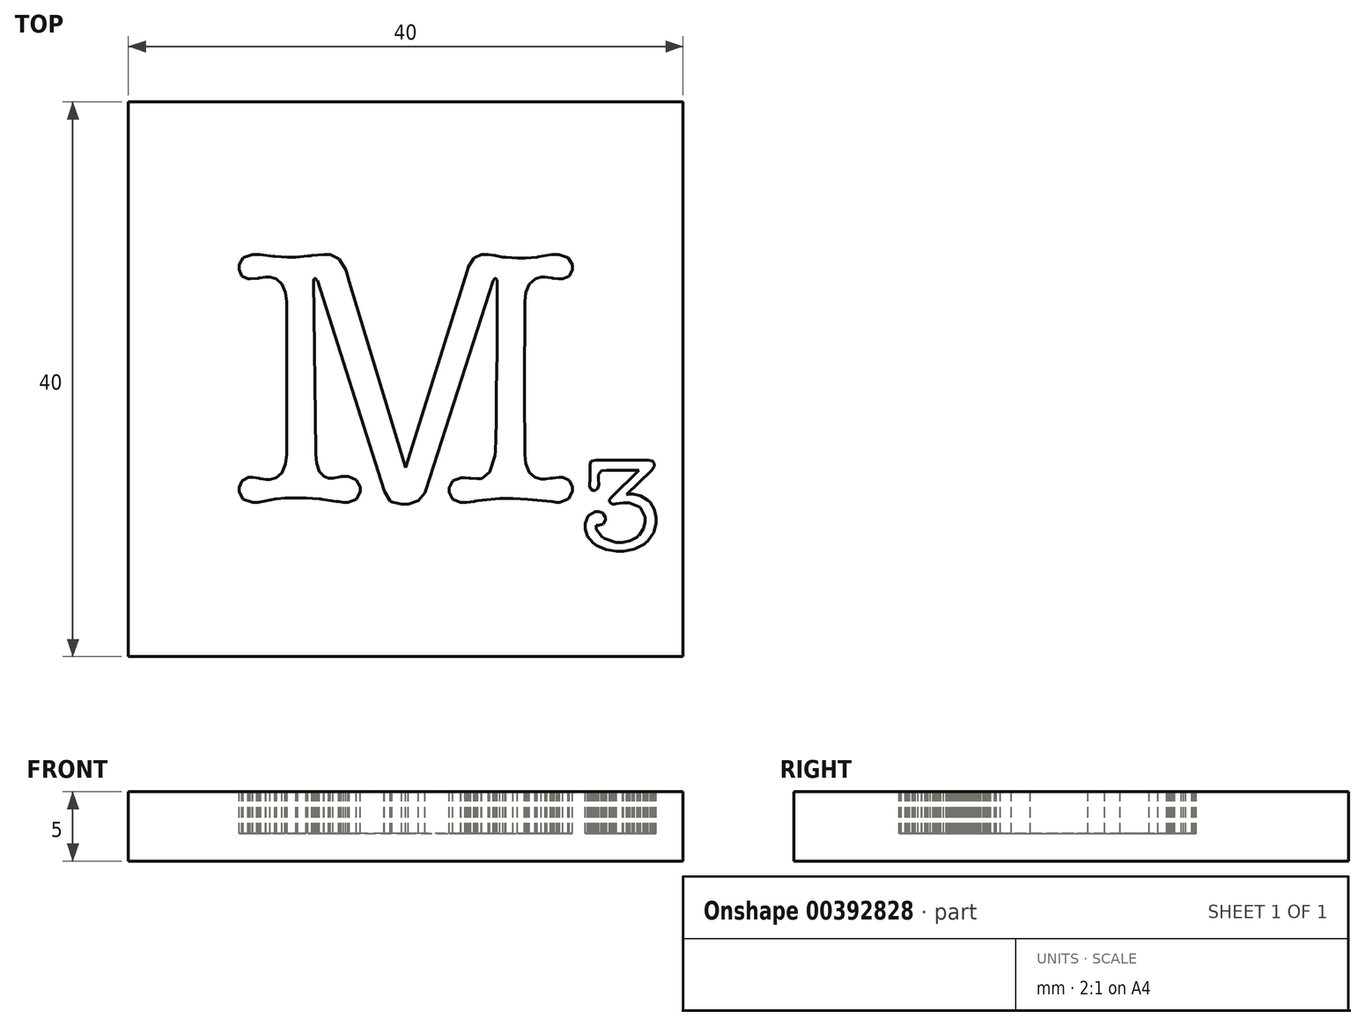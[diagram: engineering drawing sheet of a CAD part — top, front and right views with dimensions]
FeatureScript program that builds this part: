
annotation { "Feature Type Name" : "Feature", "Feature Type Description" : "" }
export const myFeature = defineFeature(function(context is Context, id is Id, definition is map)
    precondition{}
    {
        {
            var Q0;
            Q0=qCreatedBy(makeId("Top.planeOp"),FACE);
            var sketch = newSketch(context, id + "F0", { "sketchPlane" : qUnion([Q0])});
            skLineSegment(sketch, "E0.bottom", {"start": v(20, -20) * mm, "end": v(-20, -20) * mm});
            skLineSegment(sketch, "E0.top", {"start": v(20, 20) * mm, "end": v(-20, 20) * mm});
            skLineSegment(sketch, "E0.left", {"start": v(20, -20) * mm, "end": v(20, 20) * mm});
            skLineSegment(sketch, "E0.right", {"start": v(-20, -20) * mm, "end": v(-20, 20) * mm});
            skPoint(sketch, "E0.middle", {"position": v(0, 0) * mm});
            skSolve(sketch);
        }
        {
            var Q0;
            Q0=makeQuery(id+"F0.imprint","IMPRINT",FACE,{"disambiguationData":[TD([[makeQuery(id+"F0.imprint","IMPRINT",EDGE,{"derivedFrom":sQuery(id+"F0.wireOp",EDGE,"E0.bottom")}),-1.0]])]});
            extrude(context, id + "F1", {"entities" : qUnion([Q0]), "depth" : -5 * mm});
        }
        {
            var Q0;
            Q0=qCreatedBy(makeId("Top.planeOp"),FACE);
            var sketch = newSketch(context, id + "F2", { "sketchPlane" : qUnion([Q0])});
            skLineSegment(sketch, "E1", {"start": v(-4.09, 7.02) * mm, "end": v(-0.01, -6.36) * mm});
            skLineSegment(sketch, "E2", {"start": v(-0.01, -6.36) * mm, "end": v(4.46, 7.9) * mm});
            skLineSegment(sketch, "E3", {"start": v(4.46, 7.9) * mm, "end": v(4.51, 8.08) * mm});
            skLineSegment(sketch, "E4", {"start": v(4.51, 8.08) * mm, "end": v(4.93, 8.73) * mm});
            skLineSegment(sketch, "E5", {"start": v(4.93, 8.73) * mm, "end": v(5.47, 9) * mm});
            skLineSegment(sketch, "E6", {"start": v(5.47, 9) * mm, "end": v(5.65, 9) * mm});
            skLineSegment(sketch, "E7", {"start": v(5.65, 9) * mm, "end": v(5.78, 9) * mm});
            skLineSegment(sketch, "E8", {"start": v(5.78, 9) * mm, "end": v(5.95, 9) * mm});
            skLineSegment(sketch, "E9", {"start": v(5.95, 9) * mm, "end": v(6.4, 8.94) * mm});
            skLineSegment(sketch, "E10", {"start": v(6.4, 8.94) * mm, "end": v(6.47, 8.93) * mm});
            skLineSegment(sketch, "E11", {"start": v(6.47, 8.93) * mm, "end": v(6.56, 8.9) * mm});
            skLineSegment(sketch, "E12", {"start": v(6.56, 8.9) * mm, "end": v(7, 8.8) * mm});
            skLineSegment(sketch, "E13", {"start": v(7, 8.8) * mm, "end": v(7.16, 8.8) * mm});
            skLineSegment(sketch, "E14", {"start": v(7.16, 8.8) * mm, "end": v(7.23, 8.79) * mm});
            skLineSegment(sketch, "E15", {"start": v(7.23, 8.79) * mm, "end": v(8.05, 8.74) * mm});
            skLineSegment(sketch, "E16", {"start": v(8.05, 8.74) * mm, "end": v(8.32, 8.74) * mm});
            skLineSegment(sketch, "E17", {"start": v(8.32, 8.74) * mm, "end": v(8.63, 8.74) * mm});
            skLineSegment(sketch, "E18", {"start": v(8.63, 8.74) * mm, "end": v(9.49, 8.81) * mm});
            skLineSegment(sketch, "E19", {"start": v(9.49, 8.81) * mm, "end": v(9.56, 8.82) * mm});
            skLineSegment(sketch, "E20", {"start": v(9.56, 8.82) * mm, "end": v(10.5, 8.98) * mm});
            skLineSegment(sketch, "E21", {"start": v(10.5, 8.98) * mm, "end": v(10.5, 8.99) * mm});
            skLineSegment(sketch, "E22", {"start": v(10.5, 8.99) * mm, "end": v(10.73, 9) * mm});
            skLineSegment(sketch, "E23", {"start": v(10.73, 9) * mm, "end": v(10.8, 9) * mm});
            skLineSegment(sketch, "E24", {"start": v(10.8, 9) * mm, "end": v(11.03, 9) * mm});
            skLineSegment(sketch, "E25", {"start": v(11.03, 9) * mm, "end": v(11.72, 8.78) * mm});
            skLineSegment(sketch, "E26", {"start": v(11.72, 8.78) * mm, "end": v(12.03, 8.26) * mm});
            skLineSegment(sketch, "E27", {"start": v(12.03, 8.26) * mm, "end": v(12.03, 8.08) * mm});
            skLineSegment(sketch, "E28", {"start": v(12.03, 8.08) * mm, "end": v(12.03, 7.92) * mm});
            skLineSegment(sketch, "E29", {"start": v(12.03, 7.92) * mm, "end": v(11.81, 7.45) * mm});
            skLineSegment(sketch, "E30", {"start": v(11.81, 7.45) * mm, "end": v(11.34, 7.24) * mm});
            skLineSegment(sketch, "E31", {"start": v(11.34, 7.24) * mm, "end": v(11.18, 7.24) * mm});
            skLineSegment(sketch, "E32", {"start": v(11.18, 7.24) * mm, "end": v(11.02, 7.24) * mm});
            skLineSegment(sketch, "E33", {"start": v(11.02, 7.24) * mm, "end": v(10.62, 7.3) * mm});
            skLineSegment(sketch, "E34", {"start": v(10.62, 7.3) * mm, "end": v(10.56, 7.3) * mm});
            skLineSegment(sketch, "E35", {"start": v(10.56, 7.3) * mm, "end": v(10.49, 7.31) * mm});
            skLineSegment(sketch, "E36", {"start": v(10.49, 7.31) * mm, "end": v(10.07, 7.37) * mm});
            skLineSegment(sketch, "E37", {"start": v(10.07, 7.37) * mm, "end": v(9.93, 7.37) * mm});
            skLineSegment(sketch, "E38", {"start": v(9.93, 7.37) * mm, "end": v(9.79, 7.37) * mm});
            skLineSegment(sketch, "E39", {"start": v(9.79, 7.37) * mm, "end": v(9.34, 7.25) * mm});
            skLineSegment(sketch, "E40", {"start": v(9.34, 7.25) * mm, "end": v(8.92, 6.87) * mm});
            skLineSegment(sketch, "E41", {"start": v(8.92, 6.87) * mm, "end": v(8.67, 6.25) * mm});
            skLineSegment(sketch, "E42", {"start": v(8.67, 6.25) * mm, "end": v(8.59, 5.6) * mm});
            skLineSegment(sketch, "E43", {"start": v(8.59, 5.6) * mm, "end": v(8.59, 5.38) * mm});
            skLineSegment(sketch, "E44", {"start": v(8.59, 5.38) * mm, "end": v(8.59, 3.53) * mm});
            skLineSegment(sketch, "E45", {"start": v(8.59, 3.53) * mm, "end": v(8.56, 1.2) * mm});
            skLineSegment(sketch, "E46", {"start": v(8.56, 1.2) * mm, "end": v(8.56, -1.05) * mm});
            skLineSegment(sketch, "E47", {"start": v(8.56, -1.05) * mm, "end": v(8.59, -5.22) * mm});
            skLineSegment(sketch, "E48", {"start": v(8.59, -5.22) * mm, "end": v(8.59, -5.44) * mm});
            skLineSegment(sketch, "E49", {"start": v(8.59, -5.44) * mm, "end": v(8.67, -6.1) * mm});
            skLineSegment(sketch, "E50", {"start": v(8.67, -6.1) * mm, "end": v(8.92, -6.71) * mm});
            skLineSegment(sketch, "E51", {"start": v(8.92, -6.71) * mm, "end": v(9.33, -7.09) * mm});
            skLineSegment(sketch, "E52", {"start": v(9.33, -7.09) * mm, "end": v(9.76, -7.2) * mm});
            skLineSegment(sketch, "E53", {"start": v(9.76, -7.2) * mm, "end": v(9.9, -7.2) * mm});
            skLineSegment(sketch, "E54", {"start": v(9.9, -7.2) * mm, "end": v(10.05, -7.2) * mm});
            skLineSegment(sketch, "E55", {"start": v(10.05, -7.2) * mm, "end": v(10.44, -7.14) * mm});
            skLineSegment(sketch, "E56", {"start": v(10.44, -7.14) * mm, "end": v(10.5, -7.13) * mm});
            skLineSegment(sketch, "E57", {"start": v(10.5, -7.13) * mm, "end": v(10.59, -7.12) * mm});
            skLineSegment(sketch, "E58", {"start": v(10.59, -7.12) * mm, "end": v(11.03, -7.08) * mm});
            skLineSegment(sketch, "E59", {"start": v(11.03, -7.08) * mm, "end": v(11.18, -7.08) * mm});
            skLineSegment(sketch, "E60", {"start": v(11.18, -7.08) * mm, "end": v(11.34, -7.08) * mm});
            skLineSegment(sketch, "E61", {"start": v(11.34, -7.08) * mm, "end": v(11.81, -7.29) * mm});
            skLineSegment(sketch, "E62", {"start": v(11.81, -7.29) * mm, "end": v(12.03, -7.76) * mm});
            skLineSegment(sketch, "E63", {"start": v(12.03, -7.76) * mm, "end": v(12.03, -7.92) * mm});
            skLineSegment(sketch, "E64", {"start": v(12.03, -7.92) * mm, "end": v(12.03, -8.1) * mm});
            skLineSegment(sketch, "E65", {"start": v(12.03, -8.1) * mm, "end": v(11.74, -8.64) * mm});
            skLineSegment(sketch, "E66", {"start": v(11.74, -8.64) * mm, "end": v(11.1, -8.88) * mm});
            skLineSegment(sketch, "E67", {"start": v(11.1, -8.88) * mm, "end": v(10.89, -8.88) * mm});
            skLineSegment(sketch, "E68", {"start": v(10.89, -8.88) * mm, "end": v(10.56, -8.83) * mm});
            skLineSegment(sketch, "E69", {"start": v(10.56, -8.83) * mm, "end": v(10.5, -8.82) * mm});
            skLineSegment(sketch, "E70", {"start": v(10.5, -8.82) * mm, "end": v(10.19, -8.79) * mm});
            skLineSegment(sketch, "E71", {"start": v(10.19, -8.79) * mm, "end": v(8.8, -8.66) * mm});
            skLineSegment(sketch, "E72", {"start": v(8.8, -8.66) * mm, "end": v(7.75, -8.61) * mm});
            skLineSegment(sketch, "E73", {"start": v(7.75, -8.61) * mm, "end": v(7.4, -8.61) * mm});
            skLineSegment(sketch, "E74", {"start": v(7.4, -8.61) * mm, "end": v(6.8, -8.61) * mm});
            skLineSegment(sketch, "E75", {"start": v(6.8, -8.61) * mm, "end": v(5.2, -8.77) * mm});
            skLineSegment(sketch, "E76", {"start": v(5.2, -8.77) * mm, "end": v(5.01, -8.8) * mm});
            skLineSegment(sketch, "E77", {"start": v(5.01, -8.8) * mm, "end": v(4.93, -8.8) * mm});
            skLineSegment(sketch, "E78", {"start": v(4.93, -8.8) * mm, "end": v(4.36, -8.88) * mm});
            skLineSegment(sketch, "E79", {"start": v(4.36, -8.88) * mm, "end": v(4.17, -8.88) * mm});
            skLineSegment(sketch, "E80", {"start": v(4.17, -8.88) * mm, "end": v(3.97, -8.88) * mm});
            skLineSegment(sketch, "E81", {"start": v(3.97, -8.88) * mm, "end": v(3.4, -8.66) * mm});
            skLineSegment(sketch, "E82", {"start": v(3.4, -8.66) * mm, "end": v(3.13, -8.17) * mm});
            skLineSegment(sketch, "E83", {"start": v(3.13, -8.17) * mm, "end": v(3.13, -8) * mm});
            skLineSegment(sketch, "E84", {"start": v(3.13, -8) * mm, "end": v(3.13, -7.83) * mm});
            skLineSegment(sketch, "E85", {"start": v(3.13, -7.83) * mm, "end": v(3.4, -7.33) * mm});
            skLineSegment(sketch, "E86", {"start": v(3.4, -7.33) * mm, "end": v(4, -7.1) * mm});
            skLineSegment(sketch, "E87", {"start": v(4, -7.1) * mm, "end": v(4.2, -7.1) * mm});
            skLineSegment(sketch, "E88", {"start": v(4.2, -7.1) * mm, "end": v(4.3, -7.1) * mm});
            skLineSegment(sketch, "E89", {"start": v(4.3, -7.1) * mm, "end": v(4.57, -7.13) * mm});
            skLineSegment(sketch, "E90", {"start": v(4.57, -7.13) * mm, "end": v(4.59, -7.13) * mm});
            skLineSegment(sketch, "E91", {"start": v(4.59, -7.13) * mm, "end": v(4.69, -7.14) * mm});
            skLineSegment(sketch, "E92", {"start": v(4.69, -7.14) * mm, "end": v(5.13, -7.18) * mm});
            skLineSegment(sketch, "E93", {"start": v(5.13, -7.18) * mm, "end": v(5.28, -7.18) * mm});
            skLineSegment(sketch, "E94", {"start": v(5.28, -7.18) * mm, "end": v(5.47, -7.18) * mm});
            skLineSegment(sketch, "E95", {"start": v(5.47, -7.18) * mm, "end": v(6.05, -6.69) * mm});
            skLineSegment(sketch, "E96", {"start": v(6.05, -6.69) * mm, "end": v(6.43, -5.53) * mm});
            skLineSegment(sketch, "E97", {"start": v(6.43, -5.53) * mm, "end": v(6.47, -5.2) * mm});
            skLineSegment(sketch, "E98", {"start": v(6.47, -5.2) * mm, "end": v(6.48, -5.13) * mm});
            skLineSegment(sketch, "E99", {"start": v(6.48, -5.13) * mm, "end": v(6.5, -4.31) * mm});
            skLineSegment(sketch, "E100", {"start": v(6.5, -4.31) * mm, "end": v(6.52, -2.95) * mm});
            skLineSegment(sketch, "E101", {"start": v(6.52, -2.95) * mm, "end": v(6.52, -2.5) * mm});
            skLineSegment(sketch, "E102", {"start": v(6.52, -2.5) * mm, "end": v(6.52, -2.23) * mm});
            skLineSegment(sketch, "E103", {"start": v(6.52, -2.23) * mm, "end": v(6.53, -1.43) * mm});
            skLineSegment(sketch, "E104", {"start": v(6.53, -1.43) * mm, "end": v(6.54, -0.24) * mm});
            skLineSegment(sketch, "E105", {"start": v(6.54, -0.24) * mm, "end": v(6.55, 0.04) * mm});
            skLineSegment(sketch, "E106", {"start": v(6.55, 0.04) * mm, "end": v(6.6, 2.42) * mm});
            skLineSegment(sketch, "E107", {"start": v(6.6, 2.42) * mm, "end": v(6.6, 7.1) * mm});
            skLineSegment(sketch, "E108", {"start": v(6.6, 7.1) * mm, "end": v(6.6, 7.14) * mm});
            skLineSegment(sketch, "E109", {"start": v(6.6, 7.14) * mm, "end": v(6.5, 7.26) * mm});
            skLineSegment(sketch, "E110", {"start": v(6.5, 7.26) * mm, "end": v(6.47, 7.26) * mm});
            skLineSegment(sketch, "E111", {"start": v(6.47, 7.26) * mm, "end": v(6.43, 7.26) * mm});
            skLineSegment(sketch, "E112", {"start": v(6.43, 7.26) * mm, "end": v(6.32, 7.13) * mm});
            skLineSegment(sketch, "E113", {"start": v(6.32, 7.13) * mm, "end": v(6.3, 7.1) * mm});
            skLineSegment(sketch, "E114", {"start": v(6.3, 7.1) * mm, "end": v(1.44, -8) * mm});
            skLineSegment(sketch, "E115", {"start": v(1.44, -8) * mm, "end": v(1.39, -8.17) * mm});
            skLineSegment(sketch, "E116", {"start": v(1.39, -8.17) * mm, "end": v(0.91, -8.76) * mm});
            skLineSegment(sketch, "E117", {"start": v(0.91, -8.76) * mm, "end": v(0.2, -9) * mm});
            skLineSegment(sketch, "E118", {"start": v(0.2, -9) * mm, "end": v(-0.04, -9) * mm});
            skLineSegment(sketch, "E119", {"start": v(-0.04, -9) * mm, "end": v(-0.3, -9) * mm});
            skLineSegment(sketch, "E120", {"start": v(-0.3, -9) * mm, "end": v(-1, -8.84) * mm});
            skLineSegment(sketch, "E121", {"start": v(-1, -8.84) * mm, "end": v(-1.06, -8.81) * mm});
            skLineSegment(sketch, "E122", {"start": v(-1.06, -8.81) * mm, "end": v(-1.11, -8.78) * mm});
            skLineSegment(sketch, "E123", {"start": v(-1.11, -8.78) * mm, "end": v(-1.54, -8.1) * mm});
            skLineSegment(sketch, "E124", {"start": v(-1.54, -8.1) * mm, "end": v(-1.57, -8) * mm});
            skLineSegment(sketch, "E125", {"start": v(-1.57, -8) * mm, "end": v(-6.36, 7.1) * mm});
            skLineSegment(sketch, "E126", {"start": v(-6.36, 7.1) * mm, "end": v(-6.38, 7.13) * mm});
            skLineSegment(sketch, "E127", {"start": v(-6.38, 7.13) * mm, "end": v(-6.5, 7.26) * mm});
            skLineSegment(sketch, "E128", {"start": v(-6.5, 7.26) * mm, "end": v(-6.55, 7.26) * mm});
            skLineSegment(sketch, "E129", {"start": v(-6.55, 7.26) * mm, "end": v(-6.58, 7.26) * mm});
            skLineSegment(sketch, "E130", {"start": v(-6.58, 7.26) * mm, "end": v(-6.66, 7.14) * mm});
            skLineSegment(sketch, "E131", {"start": v(-6.66, 7.14) * mm, "end": v(-6.66, 7.1) * mm});
            skLineSegment(sketch, "E132", {"start": v(-6.66, 7.1) * mm, "end": v(-6.5, -5.2) * mm});
            skLineSegment(sketch, "E133", {"start": v(-6.5, -5.2) * mm, "end": v(-6.5, -5.4) * mm});
            skLineSegment(sketch, "E134", {"start": v(-6.5, -5.4) * mm, "end": v(-6.42, -6.04) * mm});
            skLineSegment(sketch, "E135", {"start": v(-6.42, -6.04) * mm, "end": v(-6.22, -6.65) * mm});
            skLineSegment(sketch, "E136", {"start": v(-6.22, -6.65) * mm, "end": v(-5.9, -7) * mm});
            skLineSegment(sketch, "E137", {"start": v(-5.9, -7) * mm, "end": v(-5.55, -7.13) * mm});
            skLineSegment(sketch, "E138", {"start": v(-5.55, -7.13) * mm, "end": v(-5.44, -7.13) * mm});
            skLineSegment(sketch, "E139", {"start": v(-5.44, -7.13) * mm, "end": v(-5.24, -7.13) * mm});
            skLineSegment(sketch, "E140", {"start": v(-5.24, -7.13) * mm, "end": v(-4.73, -7.04) * mm});
            skLineSegment(sketch, "E141", {"start": v(-4.73, -7.04) * mm, "end": v(-4.64, -7.02) * mm});
            skLineSegment(sketch, "E142", {"start": v(-4.64, -7.02) * mm, "end": v(-4.33, -7.02) * mm});
            skLineSegment(sketch, "E143", {"start": v(-4.33, -7.02) * mm, "end": v(-4.13, -7.02) * mm});
            skLineSegment(sketch, "E144", {"start": v(-4.13, -7.02) * mm, "end": v(-3.55, -7.26) * mm});
            skLineSegment(sketch, "E145", {"start": v(-3.55, -7.26) * mm, "end": v(-3.3, -7.78) * mm});
            skLineSegment(sketch, "E146", {"start": v(-3.3, -7.78) * mm, "end": v(-3.3, -7.95) * mm});
            skLineSegment(sketch, "E147", {"start": v(-3.3, -7.95) * mm, "end": v(-3.3, -8.12) * mm});
            skLineSegment(sketch, "E148", {"start": v(-3.3, -8.12) * mm, "end": v(-3.56, -8.65) * mm});
            skLineSegment(sketch, "E149", {"start": v(-3.56, -8.65) * mm, "end": v(-4.15, -8.88) * mm});
            skLineSegment(sketch, "E150", {"start": v(-4.15, -8.88) * mm, "end": v(-4.35, -8.88) * mm});
            skLineSegment(sketch, "E151", {"start": v(-4.35, -8.88) * mm, "end": v(-4.5, -8.88) * mm});
            skLineSegment(sketch, "E152", {"start": v(-4.5, -8.88) * mm, "end": v(-4.85, -8.83) * mm});
            skLineSegment(sketch, "E153", {"start": v(-4.85, -8.83) * mm, "end": v(-4.9, -8.82) * mm});
            skLineSegment(sketch, "E154", {"start": v(-4.9, -8.82) * mm, "end": v(-5, -8.81) * mm});
            skLineSegment(sketch, "E155", {"start": v(-5, -8.81) * mm, "end": v(-6.04, -8.65) * mm});
            skLineSegment(sketch, "E156", {"start": v(-6.04, -8.65) * mm, "end": v(-6.15, -8.64) * mm});
            skLineSegment(sketch, "E157", {"start": v(-6.15, -8.64) * mm, "end": v(-6.24, -8.62) * mm});
            skLineSegment(sketch, "E158", {"start": v(-6.24, -8.62) * mm, "end": v(-7.19, -8.56) * mm});
            skLineSegment(sketch, "E159", {"start": v(-7.19, -8.56) * mm, "end": v(-7.5, -8.56) * mm});
            skLineSegment(sketch, "E160", {"start": v(-7.5, -8.56) * mm, "end": v(-7.8, -8.56) * mm});
            skLineSegment(sketch, "E161", {"start": v(-7.8, -8.56) * mm, "end": v(-8.7, -8.58) * mm});
            skLineSegment(sketch, "E162", {"start": v(-8.7, -8.58) * mm, "end": v(-9.3, -8.62) * mm});
            skLineSegment(sketch, "E163", {"start": v(-9.3, -8.62) * mm, "end": v(-9.38, -8.64) * mm});
            skLineSegment(sketch, "E164", {"start": v(-9.38, -8.64) * mm, "end": v(-10.5, -8.85) * mm});
            skLineSegment(sketch, "E165", {"start": v(-10.5, -8.85) * mm, "end": v(-10.53, -8.85) * mm});
            skLineSegment(sketch, "E166", {"start": v(-10.53, -8.85) * mm, "end": v(-10.63, -8.87) * mm});
            skLineSegment(sketch, "E167", {"start": v(-10.63, -8.87) * mm, "end": v(-10.65, -8.88) * mm});
            skLineSegment(sketch, "E168", {"start": v(-10.65, -8.88) * mm, "end": v(-10.8, -8.88) * mm});
            skLineSegment(sketch, "E169", {"start": v(-10.8, -8.88) * mm, "end": v(-11.04, -8.88) * mm});
            skLineSegment(sketch, "E170", {"start": v(-11.04, -8.88) * mm, "end": v(-11.72, -8.65) * mm});
            skLineSegment(sketch, "E171", {"start": v(-11.72, -8.65) * mm, "end": v(-12.03, -8.12) * mm});
            skLineSegment(sketch, "E172", {"start": v(-12.03, -8.12) * mm, "end": v(-12.03, -7.95) * mm});
            skLineSegment(sketch, "E173", {"start": v(-12.03, -7.95) * mm, "end": v(-12.03, -7.8) * mm});
            skLineSegment(sketch, "E174", {"start": v(-12.03, -7.8) * mm, "end": v(-11.83, -7.37) * mm});
            skLineSegment(sketch, "E175", {"start": v(-11.83, -7.37) * mm, "end": v(-11.79, -7.33) * mm});
            skLineSegment(sketch, "E176", {"start": v(-11.79, -7.33) * mm, "end": v(-11.75, -7.29) * mm});
            skLineSegment(sketch, "E177", {"start": v(-11.75, -7.29) * mm, "end": v(-11.34, -7.08) * mm});
            skLineSegment(sketch, "E178", {"start": v(-11.34, -7.08) * mm, "end": v(-11.2, -7.08) * mm});
            skLineSegment(sketch, "E179", {"start": v(-11.2, -7.08) * mm, "end": v(-11.03, -7.08) * mm});
            skLineSegment(sketch, "E180", {"start": v(-11.03, -7.08) * mm, "end": v(-10.58, -7.14) * mm});
            skLineSegment(sketch, "E181", {"start": v(-10.58, -7.14) * mm, "end": v(-10.52, -7.16) * mm});
            skLineSegment(sketch, "E182", {"start": v(-10.52, -7.16) * mm, "end": v(-10.45, -7.17) * mm});
            skLineSegment(sketch, "E183", {"start": v(-10.45, -7.17) * mm, "end": v(-10.06, -7.24) * mm});
            skLineSegment(sketch, "E184", {"start": v(-10.06, -7.24) * mm, "end": v(-9.93, -7.24) * mm});
            skLineSegment(sketch, "E185", {"start": v(-9.93, -7.24) * mm, "end": v(-9.79, -7.24) * mm});
            skLineSegment(sketch, "E186", {"start": v(-9.79, -7.24) * mm, "end": v(-9.35, -7.11) * mm});
            skLineSegment(sketch, "E187", {"start": v(-9.35, -7.11) * mm, "end": v(-8.92, -6.74) * mm});
            skLineSegment(sketch, "E188", {"start": v(-8.92, -6.74) * mm, "end": v(-8.67, -6.12) * mm});
            skLineSegment(sketch, "E189", {"start": v(-8.67, -6.12) * mm, "end": v(-8.59, -5.47) * mm});
            skLineSegment(sketch, "E190", {"start": v(-8.59, -5.47) * mm, "end": v(-8.59, -5.25) * mm});
            skLineSegment(sketch, "E191", {"start": v(-8.59, -5.25) * mm, "end": v(-8.59, 5.38) * mm});
            skLineSegment(sketch, "E192", {"start": v(-8.59, 5.38) * mm, "end": v(-8.59, 5.6) * mm});
            skLineSegment(sketch, "E193", {"start": v(-8.59, 5.6) * mm, "end": v(-8.67, 6.25) * mm});
            skLineSegment(sketch, "E194", {"start": v(-8.67, 6.25) * mm, "end": v(-8.92, 6.87) * mm});
            skLineSegment(sketch, "E195", {"start": v(-8.92, 6.87) * mm, "end": v(-9.35, 7.25) * mm});
            skLineSegment(sketch, "E196", {"start": v(-9.35, 7.25) * mm, "end": v(-9.79, 7.37) * mm});
            skLineSegment(sketch, "E197", {"start": v(-9.79, 7.37) * mm, "end": v(-9.93, 7.37) * mm});
            skLineSegment(sketch, "E198", {"start": v(-9.93, 7.37) * mm, "end": v(-10.1, 7.37) * mm});
            skLineSegment(sketch, "E199", {"start": v(-10.1, 7.37) * mm, "end": v(-10.5, 7.31) * mm});
            skLineSegment(sketch, "E200", {"start": v(-10.5, 7.31) * mm, "end": v(-10.57, 7.3) * mm});
            skLineSegment(sketch, "E201", {"start": v(-10.57, 7.3) * mm, "end": v(-10.64, 7.3) * mm});
            skLineSegment(sketch, "E202", {"start": v(-10.64, 7.3) * mm, "end": v(-11.2, 7.24) * mm});
            skLineSegment(sketch, "E203", {"start": v(-11.2, 7.24) * mm, "end": v(-11.36, 7.24) * mm});
            skLineSegment(sketch, "E204", {"start": v(-11.36, 7.24) * mm, "end": v(-11.82, 7.45) * mm});
            skLineSegment(sketch, "E205", {"start": v(-11.82, 7.45) * mm, "end": v(-12.03, 7.92) * mm});
            skLineSegment(sketch, "E206", {"start": v(-12.03, 7.92) * mm, "end": v(-12.03, 8.08) * mm});
            skLineSegment(sketch, "E207", {"start": v(-12.03, 8.08) * mm, "end": v(-12.03, 8.26) * mm});
            skLineSegment(sketch, "E208", {"start": v(-12.03, 8.26) * mm, "end": v(-11.73, 8.78) * mm});
            skLineSegment(sketch, "E209", {"start": v(-11.73, 8.78) * mm, "end": v(-11.06, 9) * mm});
            skLineSegment(sketch, "E210", {"start": v(-11.06, 9) * mm, "end": v(-10.83, 9) * mm});
            skLineSegment(sketch, "E211", {"start": v(-10.83, 9) * mm, "end": v(-10.75, 9) * mm});
            skLineSegment(sketch, "E212", {"start": v(-10.75, 9) * mm, "end": v(-10.53, 8.99) * mm});
            skLineSegment(sketch, "E213", {"start": v(-10.53, 8.99) * mm, "end": v(-10.5, 8.98) * mm});
            skLineSegment(sketch, "E214", {"start": v(-10.5, 8.98) * mm, "end": v(-9.57, 8.88) * mm});
            skLineSegment(sketch, "E215", {"start": v(-9.57, 8.88) * mm, "end": v(-9.45, 8.86) * mm});
            skLineSegment(sketch, "E216", {"start": v(-9.45, 8.86) * mm, "end": v(-8.57, 8.8) * mm});
            skLineSegment(sketch, "E217", {"start": v(-8.57, 8.8) * mm, "end": v(-8.27, 8.8) * mm});
            skLineSegment(sketch, "E218", {"start": v(-8.27, 8.8) * mm, "end": v(-7.93, 8.8) * mm});
            skLineSegment(sketch, "E219", {"start": v(-7.93, 8.8) * mm, "end": v(-7.05, 8.89) * mm});
            skLineSegment(sketch, "E220", {"start": v(-7.05, 8.89) * mm, "end": v(-6.9, 8.9) * mm});
            skLineSegment(sketch, "E221", {"start": v(-6.9, 8.9) * mm, "end": v(-6.76, 8.92) * mm});
            skLineSegment(sketch, "E222", {"start": v(-6.76, 8.92) * mm, "end": v(-5.93, 9) * mm});
            skLineSegment(sketch, "E223", {"start": v(-5.93, 9) * mm, "end": v(-5.65, 9) * mm});
            skLineSegment(sketch, "E224", {"start": v(-5.65, 9) * mm, "end": v(-5.44, 9) * mm});
            skLineSegment(sketch, "E225", {"start": v(-5.44, 9) * mm, "end": v(-4.8, 8.69) * mm});
            skLineSegment(sketch, "E226", {"start": v(-4.8, 8.69) * mm, "end": v(-4.33, 7.93) * mm});
            skLineSegment(sketch, "E227", {"start": v(-4.33, 7.93) * mm, "end": v(-4.27, 7.71) * mm});
            skLineSegment(sketch, "E228", {"start": v(-4.27, 7.71) * mm, "end": v(-4.09, 7.02) * mm});
            skSolve(sketch);
        }
        {
            var Q0;
            Q0=qCreatedBy(makeId("Top.planeOp"),FACE);
            var sketch = newSketch(context, id + "F3", { "sketchPlane" : qUnion([Q0])});
            skLineSegment(sketch, "E229", {"start": v(14.85, -8.5) * mm, "end": v(16.83, -6.56) * mm});
            skLineSegment(sketch, "E230", {"start": v(16.83, -6.56) * mm, "end": v(14.62, -6.56) * mm});
            skLineSegment(sketch, "E231", {"start": v(14.62, -6.56) * mm, "end": v(14.5, -6.56) * mm});
            skLineSegment(sketch, "E232", {"start": v(14.5, -6.56) * mm, "end": v(14.15, -6.6) * mm});
            skLineSegment(sketch, "E233", {"start": v(14.15, -6.6) * mm, "end": v(14.13, -6.6) * mm});
            skLineSegment(sketch, "E234", {"start": v(14.13, -6.6) * mm, "end": v(14.09, -6.62) * mm});
            skLineSegment(sketch, "E235", {"start": v(14.09, -6.62) * mm, "end": v(13.89, -6.9) * mm});
            skLineSegment(sketch, "E236", {"start": v(13.89, -6.9) * mm, "end": v(13.89, -6.98) * mm});
            skLineSegment(sketch, "E237", {"start": v(13.89, -6.98) * mm, "end": v(13.89, -7.05) * mm});
            skLineSegment(sketch, "E238", {"start": v(13.89, -7.05) * mm, "end": v(13.9, -7.23) * mm});
            skLineSegment(sketch, "E239", {"start": v(13.9, -7.23) * mm, "end": v(13.9, -7.26) * mm});
            skLineSegment(sketch, "E240", {"start": v(13.9, -7.26) * mm, "end": v(13.9, -7.29) * mm});
            skLineSegment(sketch, "E241", {"start": v(13.9, -7.29) * mm, "end": v(13.93, -7.47) * mm});
            skLineSegment(sketch, "E242", {"start": v(13.93, -7.47) * mm, "end": v(13.93, -7.53) * mm});
            skLineSegment(sketch, "E243", {"start": v(13.93, -7.53) * mm, "end": v(13.93, -7.63) * mm});
            skLineSegment(sketch, "E244", {"start": v(13.93, -7.63) * mm, "end": v(13.84, -7.9) * mm});
            skLineSegment(sketch, "E245", {"start": v(13.84, -7.9) * mm, "end": v(13.65, -8.03) * mm});
            skLineSegment(sketch, "E246", {"start": v(13.65, -8.03) * mm, "end": v(13.6, -8.03) * mm});
            skLineSegment(sketch, "E247", {"start": v(13.6, -8.03) * mm, "end": v(13.53, -8.03) * mm});
            skLineSegment(sketch, "E248", {"start": v(13.53, -8.03) * mm, "end": v(13.35, -7.93) * mm});
            skLineSegment(sketch, "E249", {"start": v(13.35, -7.93) * mm, "end": v(13.27, -7.7) * mm});
            skLineSegment(sketch, "E250", {"start": v(13.27, -7.7) * mm, "end": v(13.27, -7.62) * mm});
            skLineSegment(sketch, "E251", {"start": v(13.27, -7.62) * mm, "end": v(13.27, -7.53) * mm});
            skLineSegment(sketch, "E252", {"start": v(13.27, -7.53) * mm, "end": v(13.28, -7.3) * mm});
            skLineSegment(sketch, "E253", {"start": v(13.28, -7.3) * mm, "end": v(13.28, -7.27) * mm});
            skLineSegment(sketch, "E254", {"start": v(13.28, -7.27) * mm, "end": v(13.28, -7.23) * mm});
            skLineSegment(sketch, "E255", {"start": v(13.28, -7.23) * mm, "end": v(13.3, -6.92) * mm});
            skLineSegment(sketch, "E256", {"start": v(13.3, -6.92) * mm, "end": v(13.3, -6.82) * mm});
            skLineSegment(sketch, "E257", {"start": v(13.3, -6.82) * mm, "end": v(13.29, -6.55) * mm});
            skLineSegment(sketch, "E258", {"start": v(13.29, -6.55) * mm, "end": v(13.29, -6.52) * mm});
            skLineSegment(sketch, "E259", {"start": v(13.29, -6.52) * mm, "end": v(13.29, -6.5) * mm});
            skLineSegment(sketch, "E260", {"start": v(13.29, -6.5) * mm, "end": v(13.28, -6.3) * mm});
            skLineSegment(sketch, "E261", {"start": v(13.28, -6.3) * mm, "end": v(13.28, -6.23) * mm});
            skLineSegment(sketch, "E262", {"start": v(13.28, -6.23) * mm, "end": v(13.28, -6.15) * mm});
            skLineSegment(sketch, "E263", {"start": v(13.28, -6.15) * mm, "end": v(13.36, -5.92) * mm});
            skLineSegment(sketch, "E264", {"start": v(13.36, -5.92) * mm, "end": v(13.37, -5.9) * mm});
            skLineSegment(sketch, "E265", {"start": v(13.37, -5.9) * mm, "end": v(13.39, -5.9) * mm});
            skLineSegment(sketch, "E266", {"start": v(13.39, -5.9) * mm, "end": v(13.73, -5.85) * mm});
            skLineSegment(sketch, "E267", {"start": v(13.73, -5.85) * mm, "end": v(13.85, -5.85) * mm});
            skLineSegment(sketch, "E268", {"start": v(13.85, -5.85) * mm, "end": v(16.2, -5.85) * mm});
            skLineSegment(sketch, "E269", {"start": v(16.2, -5.85) * mm, "end": v(16.35, -5.85) * mm});
            skLineSegment(sketch, "E270", {"start": v(16.35, -5.85) * mm, "end": v(16.76, -5.83) * mm});
            skLineSegment(sketch, "E271", {"start": v(16.76, -5.83) * mm, "end": v(16.84, -5.83) * mm});
            skLineSegment(sketch, "E272", {"start": v(16.84, -5.83) * mm, "end": v(16.88, -5.83) * mm});
            skLineSegment(sketch, "E273", {"start": v(16.88, -5.83) * mm, "end": v(17.25, -5.82) * mm});
            skLineSegment(sketch, "E274", {"start": v(17.25, -5.82) * mm, "end": v(17.37, -5.82) * mm});
            skLineSegment(sketch, "E275", {"start": v(17.37, -5.82) * mm, "end": v(17.48, -5.82) * mm});
            skLineSegment(sketch, "E276", {"start": v(17.48, -5.82) * mm, "end": v(17.8, -5.9) * mm});
            skLineSegment(sketch, "E277", {"start": v(17.8, -5.9) * mm, "end": v(17.94, -6.1) * mm});
            skLineSegment(sketch, "E278", {"start": v(17.94, -6.1) * mm, "end": v(17.94, -6.16) * mm});
            skLineSegment(sketch, "E279", {"start": v(17.94, -6.16) * mm, "end": v(17.94, -6.27) * mm});
            skLineSegment(sketch, "E280", {"start": v(17.94, -6.27) * mm, "end": v(17.74, -6.57) * mm});
            skLineSegment(sketch, "E281", {"start": v(17.74, -6.57) * mm, "end": v(17.7, -6.6) * mm});
            skLineSegment(sketch, "E282", {"start": v(17.7, -6.6) * mm, "end": v(15.95, -8.3) * mm});
            skLineSegment(sketch, "E283", {"start": v(15.95, -8.3) * mm, "end": v(15.98, -8.3) * mm});
            skLineSegment(sketch, "E284", {"start": v(15.98, -8.3) * mm, "end": v(16.08, -8.29) * mm});
            skLineSegment(sketch, "E285", {"start": v(16.08, -8.29) * mm, "end": v(16.1, -8.29) * mm});
            skLineSegment(sketch, "E286", {"start": v(16.1, -8.29) * mm, "end": v(16.22, -8.29) * mm});
            skLineSegment(sketch, "E287", {"start": v(16.22, -8.29) * mm, "end": v(16.4, -8.29) * mm});
            skLineSegment(sketch, "E288", {"start": v(16.4, -8.29) * mm, "end": v(16.96, -8.41) * mm});
            skLineSegment(sketch, "E289", {"start": v(16.96, -8.41) * mm, "end": v(17.46, -8.72) * mm});
            skLineSegment(sketch, "E290", {"start": v(17.46, -8.72) * mm, "end": v(17.55, -8.8) * mm});
            skLineSegment(sketch, "E291", {"start": v(17.55, -8.8) * mm, "end": v(17.64, -8.9) * mm});
            skLineSegment(sketch, "E292", {"start": v(17.64, -8.9) * mm, "end": v(17.94, -9.4) * mm});
            skLineSegment(sketch, "E293", {"start": v(17.94, -9.4) * mm, "end": v(18.07, -9.95) * mm});
            skLineSegment(sketch, "E294", {"start": v(18.07, -9.95) * mm, "end": v(18.07, -10.13) * mm});
            skLineSegment(sketch, "E295", {"start": v(18.07, -10.13) * mm, "end": v(18.07, -10.36) * mm});
            skLineSegment(sketch, "E296", {"start": v(18.07, -10.36) * mm, "end": v(17.88, -11.05) * mm});
            skLineSegment(sketch, "E297", {"start": v(17.88, -11.05) * mm, "end": v(17.45, -11.67) * mm});
            skLineSegment(sketch, "E298", {"start": v(17.45, -11.67) * mm, "end": v(17.33, -11.78) * mm});
            skLineSegment(sketch, "E299", {"start": v(17.33, -11.78) * mm, "end": v(17.2, -11.89) * mm});
            skLineSegment(sketch, "E300", {"start": v(17.2, -11.89) * mm, "end": v(16.49, -12.26) * mm});
            skLineSegment(sketch, "E301", {"start": v(16.49, -12.26) * mm, "end": v(15.7, -12.42) * mm});
            skLineSegment(sketch, "E302", {"start": v(15.7, -12.42) * mm, "end": v(15.43, -12.42) * mm});
            skLineSegment(sketch, "E303", {"start": v(15.43, -12.42) * mm, "end": v(15.19, -12.42) * mm});
            skLineSegment(sketch, "E304", {"start": v(15.19, -12.42) * mm, "end": v(14.45, -12.29) * mm});
            skLineSegment(sketch, "E305", {"start": v(14.45, -12.29) * mm, "end": v(13.77, -11.99) * mm});
            skLineSegment(sketch, "E306", {"start": v(13.77, -11.99) * mm, "end": v(13.65, -11.9) * mm});
            skLineSegment(sketch, "E307", {"start": v(13.65, -11.9) * mm, "end": v(13.53, -11.81) * mm});
            skLineSegment(sketch, "E308", {"start": v(13.53, -11.81) * mm, "end": v(13.11, -11.32) * mm});
            skLineSegment(sketch, "E309", {"start": v(13.11, -11.32) * mm, "end": v(12.94, -10.78) * mm});
            skLineSegment(sketch, "E310", {"start": v(12.94, -10.78) * mm, "end": v(12.94, -10.6) * mm});
            skLineSegment(sketch, "E311", {"start": v(12.94, -10.6) * mm, "end": v(12.94, -10.41) * mm});
            skLineSegment(sketch, "E312", {"start": v(12.94, -10.41) * mm, "end": v(13.15, -9.9) * mm});
            skLineSegment(sketch, "E313", {"start": v(13.15, -9.9) * mm, "end": v(13.2, -9.84) * mm});
            skLineSegment(sketch, "E314", {"start": v(13.2, -9.84) * mm, "end": v(13.23, -9.79) * mm});
            skLineSegment(sketch, "E315", {"start": v(13.23, -9.79) * mm, "end": v(13.68, -9.53) * mm});
            skLineSegment(sketch, "E316", {"start": v(13.68, -9.53) * mm, "end": v(13.83, -9.53) * mm});
            skLineSegment(sketch, "E317", {"start": v(13.83, -9.53) * mm, "end": v(13.93, -9.53) * mm});
            skLineSegment(sketch, "E318", {"start": v(13.93, -9.53) * mm, "end": v(14.2, -9.66) * mm});
            skLineSegment(sketch, "E319", {"start": v(14.2, -9.66) * mm, "end": v(14.24, -9.68) * mm});
            skLineSegment(sketch, "E320", {"start": v(14.24, -9.68) * mm, "end": v(14.26, -9.7) * mm});
            skLineSegment(sketch, "E321", {"start": v(14.26, -9.7) * mm, "end": v(14.4, -9.98) * mm});
            skLineSegment(sketch, "E322", {"start": v(14.4, -9.98) * mm, "end": v(14.4, -10.07) * mm});
            skLineSegment(sketch, "E323", {"start": v(14.4, -10.07) * mm, "end": v(14.4, -10.16) * mm});
            skLineSegment(sketch, "E324", {"start": v(14.4, -10.16) * mm, "end": v(14.25, -10.42) * mm});
            skLineSegment(sketch, "E325", {"start": v(14.25, -10.42) * mm, "end": v(13.93, -10.54) * mm});
            skLineSegment(sketch, "E326", {"start": v(13.93, -10.54) * mm, "end": v(13.83, -10.54) * mm});
            skLineSegment(sketch, "E327", {"start": v(13.83, -10.54) * mm, "end": v(13.73, -10.54) * mm});
            skLineSegment(sketch, "E328", {"start": v(13.73, -10.54) * mm, "end": v(13.73, -10.6) * mm});
            skLineSegment(sketch, "E329", {"start": v(13.73, -10.6) * mm, "end": v(13.73, -10.81) * mm});
            skLineSegment(sketch, "E330", {"start": v(13.73, -10.81) * mm, "end": v(14.16, -11.36) * mm});
            skLineSegment(sketch, "E331", {"start": v(14.16, -11.36) * mm, "end": v(14.24, -11.42) * mm});
            skLineSegment(sketch, "E332", {"start": v(14.24, -11.42) * mm, "end": v(14.33, -11.48) * mm});
            skLineSegment(sketch, "E333", {"start": v(14.33, -11.48) * mm, "end": v(15.18, -11.76) * mm});
            skLineSegment(sketch, "E334", {"start": v(15.18, -11.76) * mm, "end": v(15.47, -11.76) * mm});
            skLineSegment(sketch, "E335", {"start": v(15.47, -11.76) * mm, "end": v(15.65, -11.76) * mm});
            skLineSegment(sketch, "E336", {"start": v(15.65, -11.76) * mm, "end": v(16.19, -11.65) * mm});
            skLineSegment(sketch, "E337", {"start": v(16.19, -11.65) * mm, "end": v(16.68, -11.38) * mm});
            skLineSegment(sketch, "E338", {"start": v(16.68, -11.38) * mm, "end": v(16.76, -11.3) * mm});
            skLineSegment(sketch, "E339", {"start": v(16.76, -11.3) * mm, "end": v(16.85, -11.23) * mm});
            skLineSegment(sketch, "E340", {"start": v(16.85, -11.23) * mm, "end": v(17.14, -10.8) * mm});
            skLineSegment(sketch, "E341", {"start": v(17.14, -10.8) * mm, "end": v(17.27, -10.31) * mm});
            skLineSegment(sketch, "E342", {"start": v(17.27, -10.31) * mm, "end": v(17.27, -10.15) * mm});
            skLineSegment(sketch, "E343", {"start": v(17.27, -10.15) * mm, "end": v(17.27, -9.92) * mm});
            skLineSegment(sketch, "E344", {"start": v(17.27, -9.92) * mm, "end": v(16.92, -9.22) * mm});
            skLineSegment(sketch, "E345", {"start": v(16.92, -9.22) * mm, "end": v(16.12, -8.91) * mm});
            skLineSegment(sketch, "E346", {"start": v(16.12, -8.91) * mm, "end": v(15.86, -8.91) * mm});
            skLineSegment(sketch, "E347", {"start": v(15.86, -8.91) * mm, "end": v(15.67, -8.91) * mm});
            skLineSegment(sketch, "E348", {"start": v(15.67, -8.91) * mm, "end": v(15.15, -8.99) * mm});
            skLineSegment(sketch, "E349", {"start": v(15.15, -8.99) * mm, "end": v(15.09, -9) * mm});
            skLineSegment(sketch, "E350", {"start": v(15.09, -9) * mm, "end": v(15.07, -9) * mm});
            skLineSegment(sketch, "E351", {"start": v(15.07, -9) * mm, "end": v(14.96, -9.02) * mm});
            skLineSegment(sketch, "E352", {"start": v(14.96, -9.02) * mm, "end": v(14.93, -9.02) * mm});
            skLineSegment(sketch, "E353", {"start": v(14.93, -9.02) * mm, "end": v(14.87, -9.02) * mm});
            skLineSegment(sketch, "E354", {"start": v(14.87, -9.02) * mm, "end": v(14.7, -8.83) * mm});
            skLineSegment(sketch, "E355", {"start": v(14.7, -8.83) * mm, "end": v(14.7, -8.77) * mm});
            skLineSegment(sketch, "E356", {"start": v(14.7, -8.77) * mm, "end": v(14.7, -8.7) * mm});
            skLineSegment(sketch, "E357", {"start": v(14.7, -8.7) * mm, "end": v(14.82, -8.53) * mm});
            skLineSegment(sketch, "E358", {"start": v(14.82, -8.53) * mm, "end": v(14.85, -8.5) * mm});
            skSolve(sketch);
        }
        {
            var Q0;
            Q0 = qSketchRegion(id + "F2", true);
            var Q1;
            Q1 = qSketchRegion(id + "F3", true);
            extrude(context, id + "F4", {"entities" : qUnion([Q0, Q1]), "depth" : -3 * mm});
        }
    });
